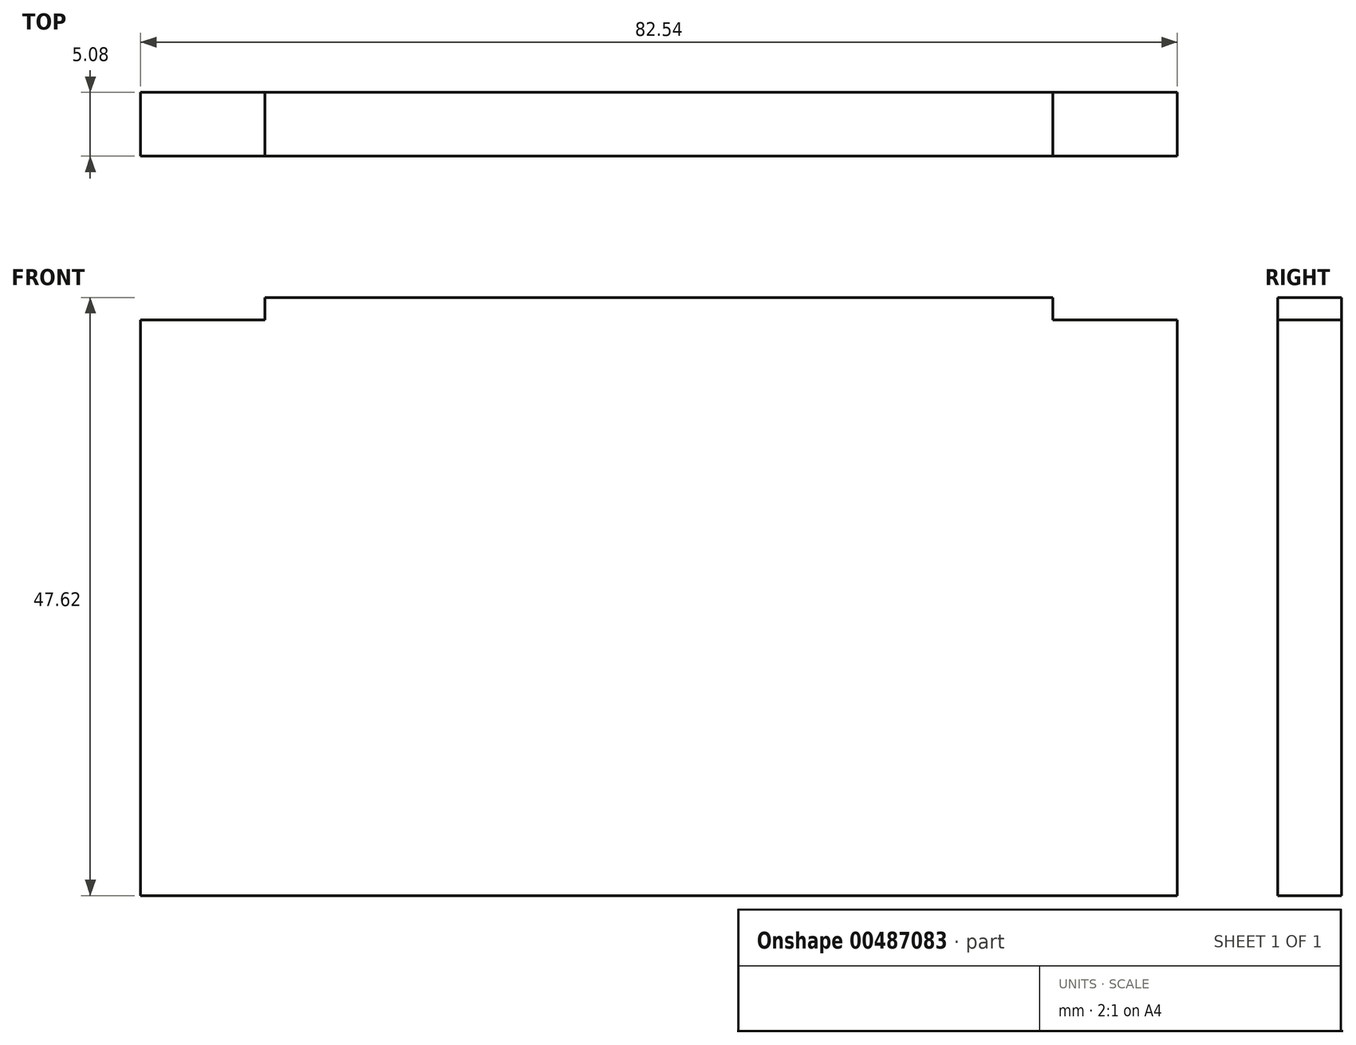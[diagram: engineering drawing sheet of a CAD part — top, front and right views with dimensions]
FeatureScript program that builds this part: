
annotation { "Feature Type Name" : "Feature", "Feature Type Description" : "" }
export const myFeature = defineFeature(function(context is Context, id is Id, definition is map)
    precondition{}
    {
        {
            var Q0;
            Q0=qCreatedBy(makeId("Front.planeOp"),FACE);
            var sketch = newSketch(context, id + "F0", { "sketchPlane" : qUnion([Q0])});
            skLineSegment(sketch, "E0.bottom", {"start": v(-31.37, 0) * mm, "end": v(31.37, 0) * mm});
            skLineSegment(sketch, "E0.top", {"start": v(-41.27, -47.63) * mm, "end": v(41.27, -47.62) * mm});
            skLineSegment(sketch, "E0.left", {"start": v(-41.28, -1.78) * mm, "end": v(-41.27, -47.62) * mm});
            skLineSegment(sketch, "E0.right", {"start": v(41.28, -1.78) * mm, "end": v(41.27, -47.62) * mm});
            skLineSegment(sketch, "E1.bottom", {"start": v(-41.28, -1.78) * mm, "end": v(-31.37, -1.78) * mm});
            skLineSegment(sketch, "E1.right", {"start": v(-31.37, -1.78) * mm, "end": v(-31.37, 0) * mm});
            skLineSegment(sketch, "E2.bottom", {"start": v(41.28, -1.78) * mm, "end": v(31.37, -1.78) * mm});
            skLineSegment(sketch, "E2.right", {"start": v(31.37, -1.78) * mm, "end": v(31.37, 0) * mm});
            skSolve(sketch);
        }
        {
            var Q0;
            Q0 = qSketchRegion(id + "F0", true);
            extrude(context, id + "F1", {"entities" : qUnion([Q0]), "depth" : 5.08 * mm});
        }
    });
